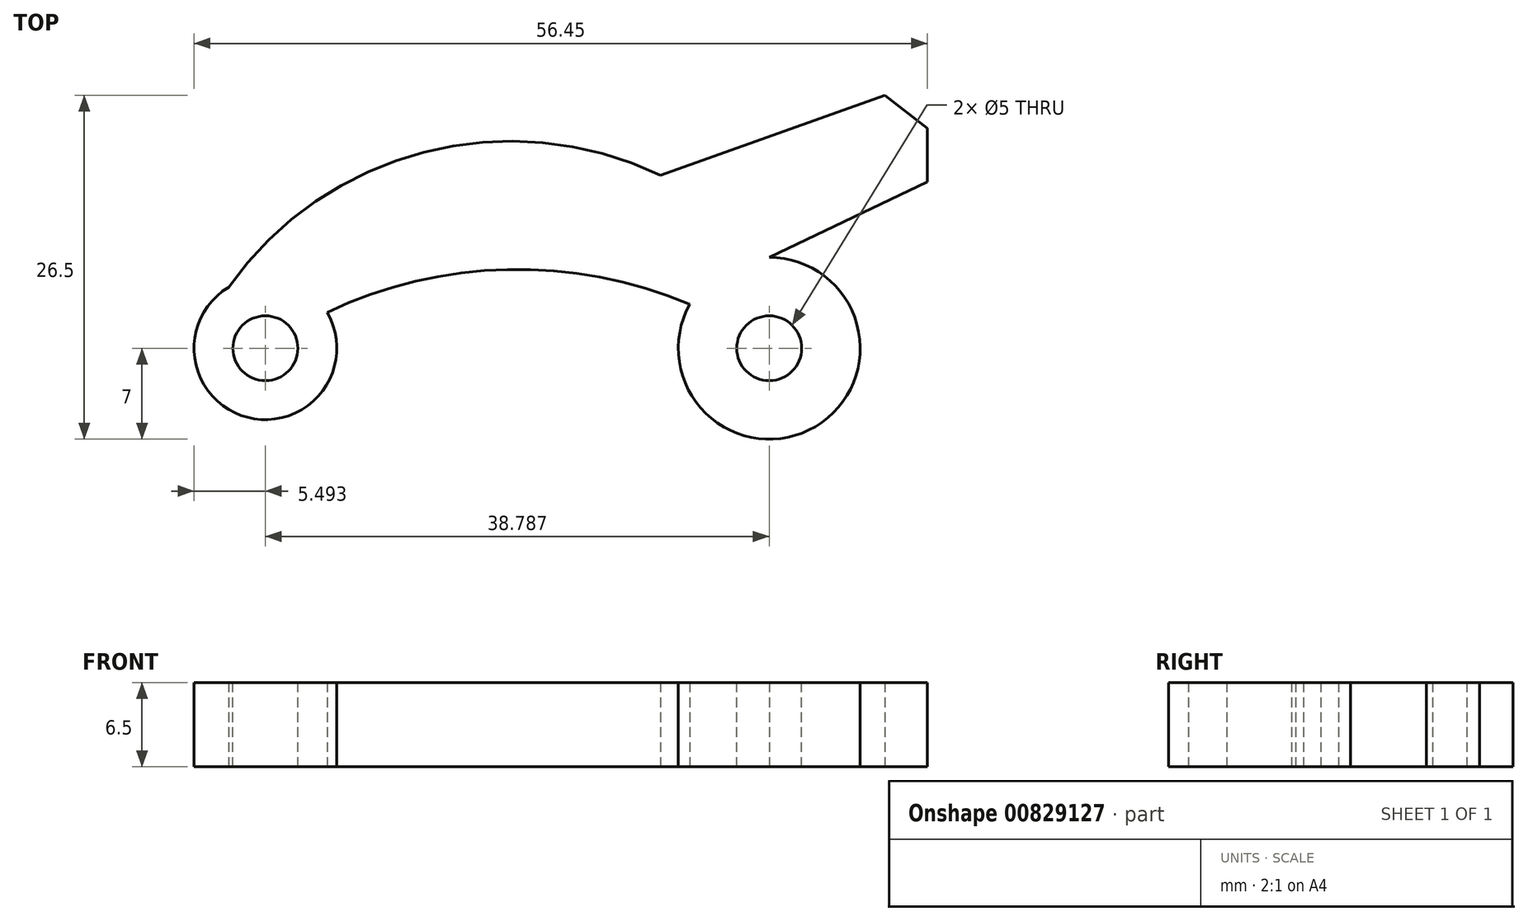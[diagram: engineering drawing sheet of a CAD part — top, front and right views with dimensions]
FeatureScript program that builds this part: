
annotation { "Feature Type Name" : "Feature", "Feature Type Description" : "" }
export const myFeature = defineFeature(function(context is Context, id is Id, definition is map)
    precondition{}
    {
        {
            var Q0;
            Q0=qCreatedBy(makeId("Top.planeOp"),FACE);
            var sketch = newSketch(context, id + "F0", { "sketchPlane" : qUnion([Q0])});
            skArc(sketch, "E0", {"start": v(-6.13, 3.38) * mm, "mid": v(3.56, -6.03) * mm, "end": v(0, 7) * mm});
            skArc(sketch, "E1", {"start": v(-41.63, 4.7) * mm, "mid": v(-40.15, -5.32) * mm, "end": v(-34.04, 2.76) * mm});
            skLineSegment(sketch, "E2", {"start": v(-38.79, 0) * mm, "end": v(0, 0) * mm, "construction": true});
            skArc(sketch, "E3", {"start": v(0, 7) * mm, "mid": v(-21.37, 15.9) * mm, "end": v(-41.63, 4.7) * mm});
            skArc(sketch, "E4", {"start": v(-6.13, 3.38) * mm, "mid": v(-20.15, 6.07) * mm, "end": v(-34.04, 2.76) * mm});
            skPoint(sketch, "E5.orphan", {"position": v(-44.28, 0) * mm});
            skLineSegment(sketch, "E6", {"start": v(-8.37, 13.32) * mm, "end": v(8.9, 19.5) * mm});
            skLineSegment(sketch, "E7", {"start": v(8.9, 19.5) * mm, "end": v(12.17, 16.94) * mm});
            skLineSegment(sketch, "E8", {"start": v(12.17, 16.94) * mm, "end": v(12.17, 12.82) * mm});
            skLineSegment(sketch, "E9", {"start": v(12.17, 12.82) * mm, "end": v(0, 7) * mm});
            skSolve(sketch);
        }
        {
            var Q0;
            Q0=makeQuery(id+"F0.imprint","IMPRINT",FACE,{"disambiguationData":[TD([[makeQuery(id+"F0.imprint","IMPRINT",EDGE,{"derivedFrom":sQuery(id+"F0.wireOp",EDGE,"E0")}),1.0]])]});
            var Q1;
            {var subQ0=sQuery(id+"F0.wireOp",EDGE,"E6");Q1=makeQuery(id+"F0.imprint","IMPRINT",FACE,{"disambiguationData":[TD([[makeQuery(id+"F0.imprint","IMPRINT",EDGE,{"derivedFrom":subQ0}),-1.0]])]});}
            extrude(context, id + "F1", {"entities" : qUnion([Q0, Q1]), "depth" : 6.5 * mm, "offsetDistance" : 25 * mm});
        }
        {
            var Q0;
            Q0=makeQuery(id+"F1.opExtrude","CAP_FACE",FACE,{"disambiguationData":[OSD([sQuery(id+"F0.wireOp",EDGE,"E0"),sQuery(id+"F0.wireOp",EDGE,"E1"),sQuery(id+"F0.wireOp",EDGE,"E3"),sQuery(id+"F0.wireOp",EDGE,"E4")])],"isStart":false});
            var sketch = newSketch(context, id + "F2", { "sketchPlane" : qUnion([Q0])});
            skCircle(sketch, "E10", {"center": v(0, 0) * mm, "radius": 2.5 * mm});
            skCircle(sketch, "E11", {"center": v(-38.79, 0) * mm, "radius": 2.5 * mm});
            skSolve(sketch);
        }
        {
            var Q0;
            Q0=makeQuery(id+"F2.imprint","IMPRINT",FACE,{"disambiguationData":[TD([[makeQuery(id+"F2.imprint","IMPRINT",EDGE,{"derivedFrom":sQuery(id+"F2.wireOp",EDGE,"E10")}),1.0]])]});
            var Q1;
            Q1=makeQuery(id+"F2.imprint","IMPRINT",FACE,{"disambiguationData":[TD([[makeQuery(id+"F2.imprint","IMPRINT",EDGE,{"derivedFrom":sQuery(id+"F2.wireOp",EDGE,"E11")}),1.0]])]});
            var Q2;
            Q2=sQuery(id+"F2.wireOp",EDGE,"E10");
            extrude(context, id + "F3", {"entities" : qUnion([Q0, Q1]), "operationType" : NewBodyOperationType.REMOVE, "surfaceEntities" : qUnion([Q2]), "oppositeDirection" : true, "depth" : 8 * mm, "offsetDistance" : 25 * mm});
        }
    });
